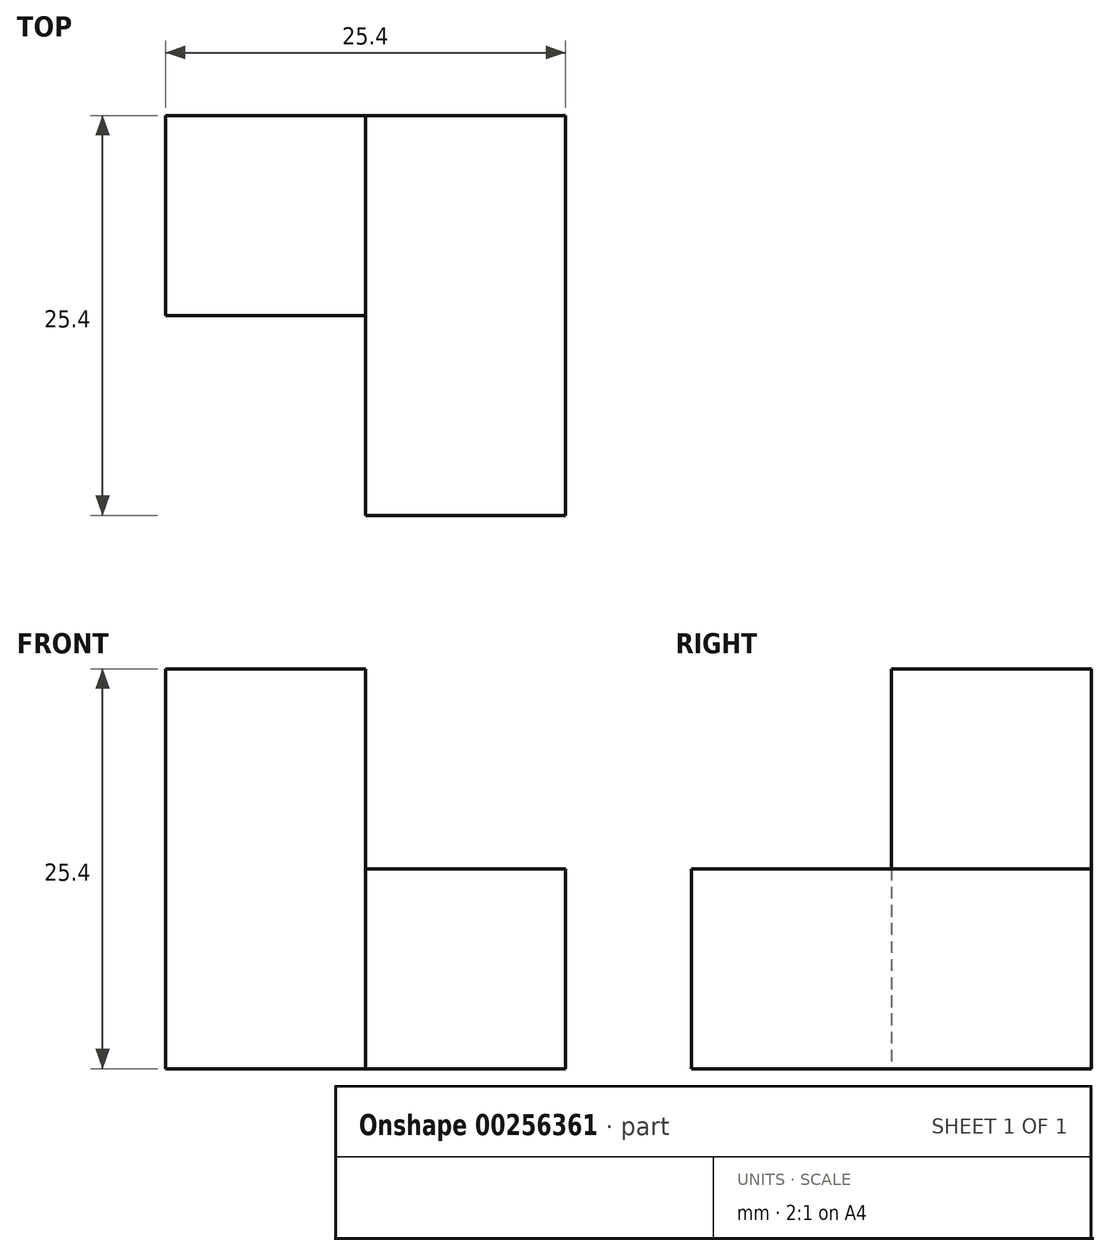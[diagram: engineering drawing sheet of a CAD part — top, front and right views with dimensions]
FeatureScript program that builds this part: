
annotation { "Feature Type Name" : "Feature", "Feature Type Description" : "" }
export const myFeature = defineFeature(function(context is Context, id is Id, definition is map)
    precondition{}
    {
        {
            var Q0;
            Q0=qCreatedBy(makeId("Front.planeOp"),FACE);
            var sketch = newSketch(context, id + "F0", { "sketchPlane" : qUnion([Q0])});
            skLineSegment(sketch, "E0", {"start": v(0, 0) * mm, "end": v(0, 25.4) * mm});
            skLineSegment(sketch, "E1", {"start": v(0, 25.4) * mm, "end": v(12.7, 25.4) * mm});
            skLineSegment(sketch, "E2", {"start": v(12.7, 25.4) * mm, "end": v(12.7, 12.7) * mm});
            skLineSegment(sketch, "E3", {"start": v(12.7, 12.7) * mm, "end": v(25.4, 12.7) * mm});
            skLineSegment(sketch, "E4", {"start": v(25.4, 12.7) * mm, "end": v(25.4, 0) * mm});
            skLineSegment(sketch, "E5", {"start": v(25.4, 0) * mm, "end": v(0, 0) * mm});
            skSolve(sketch);
        }
        {
            var Q0;
            Q0 = qSketchRegion(id + "F0", true);
            extrude(context, id + "F1", {"entities" : qUnion([Q0]), "depth" : 12.7 * mm});
        }
        {
            var Q0;
            Q0=makeQuery(id+"F1.opExtrude","CAP_FACE",FACE,{"disambiguationData":[OSD([sQuery(id+"F0.wireOp",EDGE,"E0"),sQuery(id+"F0.wireOp",EDGE,"E1"),sQuery(id+"F0.wireOp",EDGE,"E2"),sQuery(id+"F0.wireOp",EDGE,"E3"),sQuery(id+"F0.wireOp",EDGE,"E4"),sQuery(id+"F0.wireOp",EDGE,"E5")])],"isStart":false});
            var sketch = newSketch(context, id + "F2", { "sketchPlane" : qUnion([Q0])});
            skLineSegment(sketch, "E6", {"start": v(12.7, 12.7) * mm, "end": v(12.7, 0) * mm});
            skSolve(sketch);
        }
        {
            var Q0;
            {var subQ0=sQuery(id+"F2.wireOp",EDGE,"E6");Q0=makeQuery(id+"F2.imprint","IMPRINT",FACE,{"disambiguationData":[TD([[makeQuery(id+"F2.imprint","IMPRINT",EDGE,{"derivedFrom":subQ0}),1.0]])]});}
            extrude(context, id + "F3", {"entities" : qUnion([Q0]), "operationType" : NewBodyOperationType.ADD, "depth" : 12.7 * mm});
        }
    });
